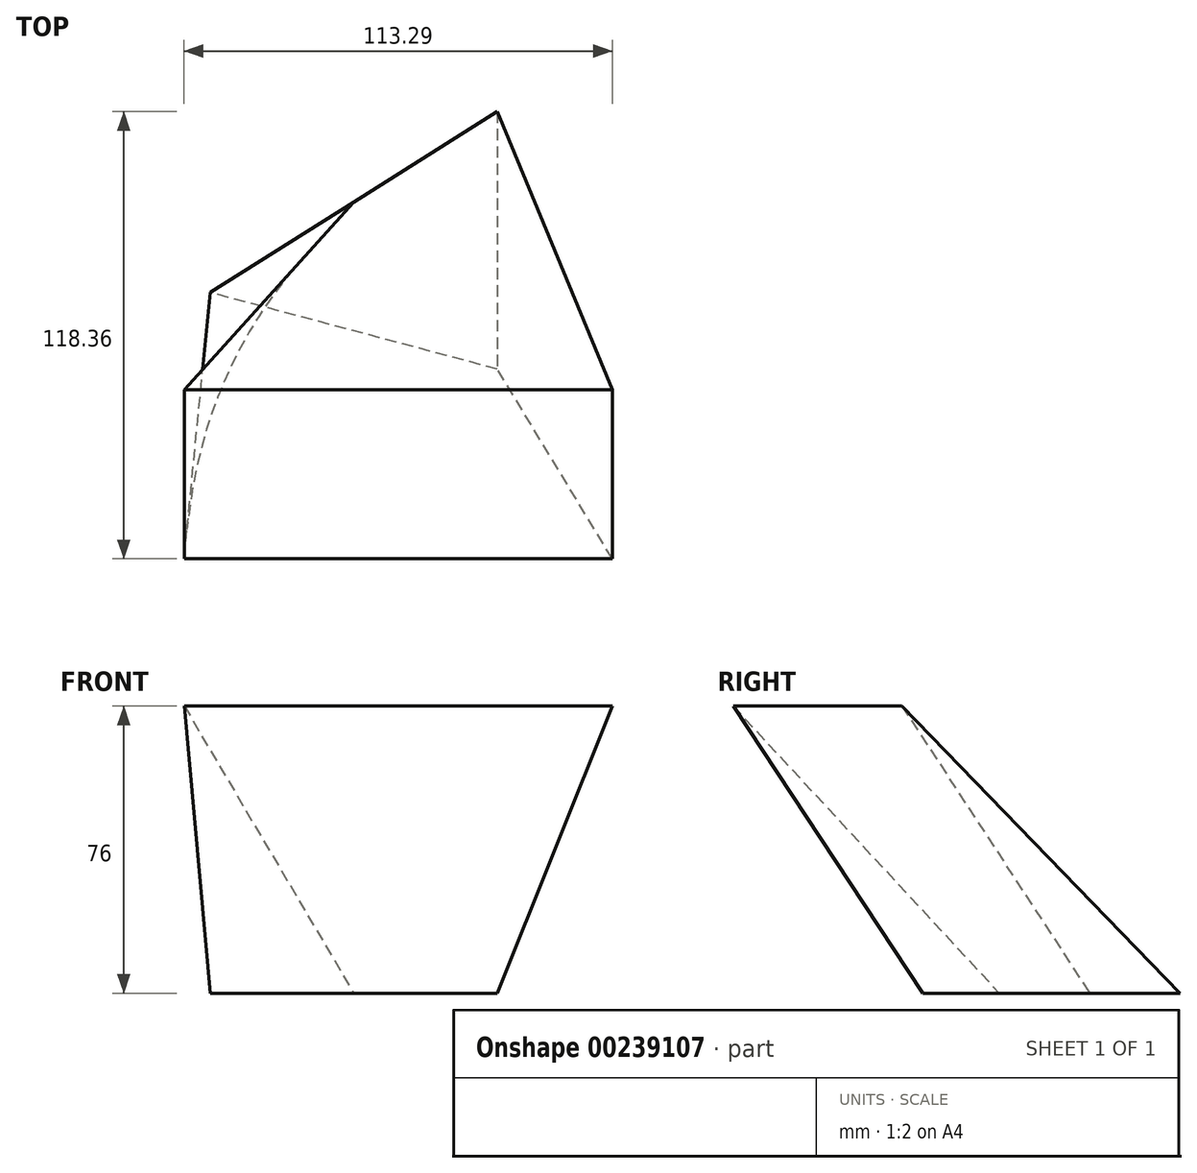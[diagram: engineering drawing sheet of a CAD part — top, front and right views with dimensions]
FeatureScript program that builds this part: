
annotation { "Feature Type Name" : "Feature", "Feature Type Description" : "" }
export const myFeature = defineFeature(function(context is Context, id is Id, definition is map)
    precondition{}
    {
        {
            var Q0;
            Q0=qCreatedBy(makeId("Top.planeOp"),FACE);
            cPlane(context, id + "F0", {"entities" : qUnion([Q0]), "cplaneType" : CPlaneType.OFFSET, "offset" : 76 * mm, "width" : 150 * mm, "height" : 150 * mm});
        }
        {
            var Q0;
            Q0=qCreatedBy(id+"F0.planeOp",FACE);
            var sketch = newSketch(context, id + "F1", { "sketchPlane" : qUnion([Q0])});
            skLineSegment(sketch, "E0.bottom", {"start": v(54.34, -61.7) * mm, "end": v(-58.95, -61.7) * mm});
            skLineSegment(sketch, "E0.top", {"start": v(54.34, -17.03) * mm, "end": v(-58.95, -17.03) * mm});
            skLineSegment(sketch, "E0.left", {"start": v(54.34, -61.7) * mm, "end": v(54.34, -17.03) * mm});
            skLineSegment(sketch, "E0.right", {"start": v(-58.95, -61.7) * mm, "end": v(-58.95, -17.03) * mm});
            skSolve(sketch);
        }
        {
            var Q0;
            Q0=qCreatedBy(makeId("Top.planeOp"),FACE);
            var sketch = newSketch(context, id + "F2", { "sketchPlane" : qUnion([Q0])});
            skLineSegment(sketch, "E1", {"start": v(-52.04, 8.75) * mm, "end": v(23.95, 56.65) * mm});
            skLineSegment(sketch, "E2", {"start": v(23.95, 56.65) * mm, "end": v(23.95, -11.51) * mm});
            skLineSegment(sketch, "E3", {"start": v(23.95, -11.51) * mm, "end": v(-52.04, 8.75) * mm});
            skSolve(sketch);
        }
        {
            var Q0;
            Q0=makeQuery(id+"F1.imprint","IMPRINT",FACE,{"disambiguationData":[TD([[makeQuery(id+"F1.imprint","IMPRINT",EDGE,{"derivedFrom":sQuery(id+"F1.wireOp",EDGE,"E0.bottom")}),-1.0]])]});
            var Q1;
            Q1=makeQuery(id+"F2.imprint","IMPRINT",FACE,{"disambiguationData":[TD([[makeQuery(id+"F2.imprint","IMPRINT",EDGE,{"derivedFrom":sQuery(id+"F2.wireOp",EDGE,"E1")}),-1.0]])]});
            loft(context, id + "F3", {"sheetProfilesArray" : [{ "sheetProfileEntities" : qUnion([Q0]) }, { "sheetProfileEntities" : qUnion([Q1]) }]});
        }
    });
